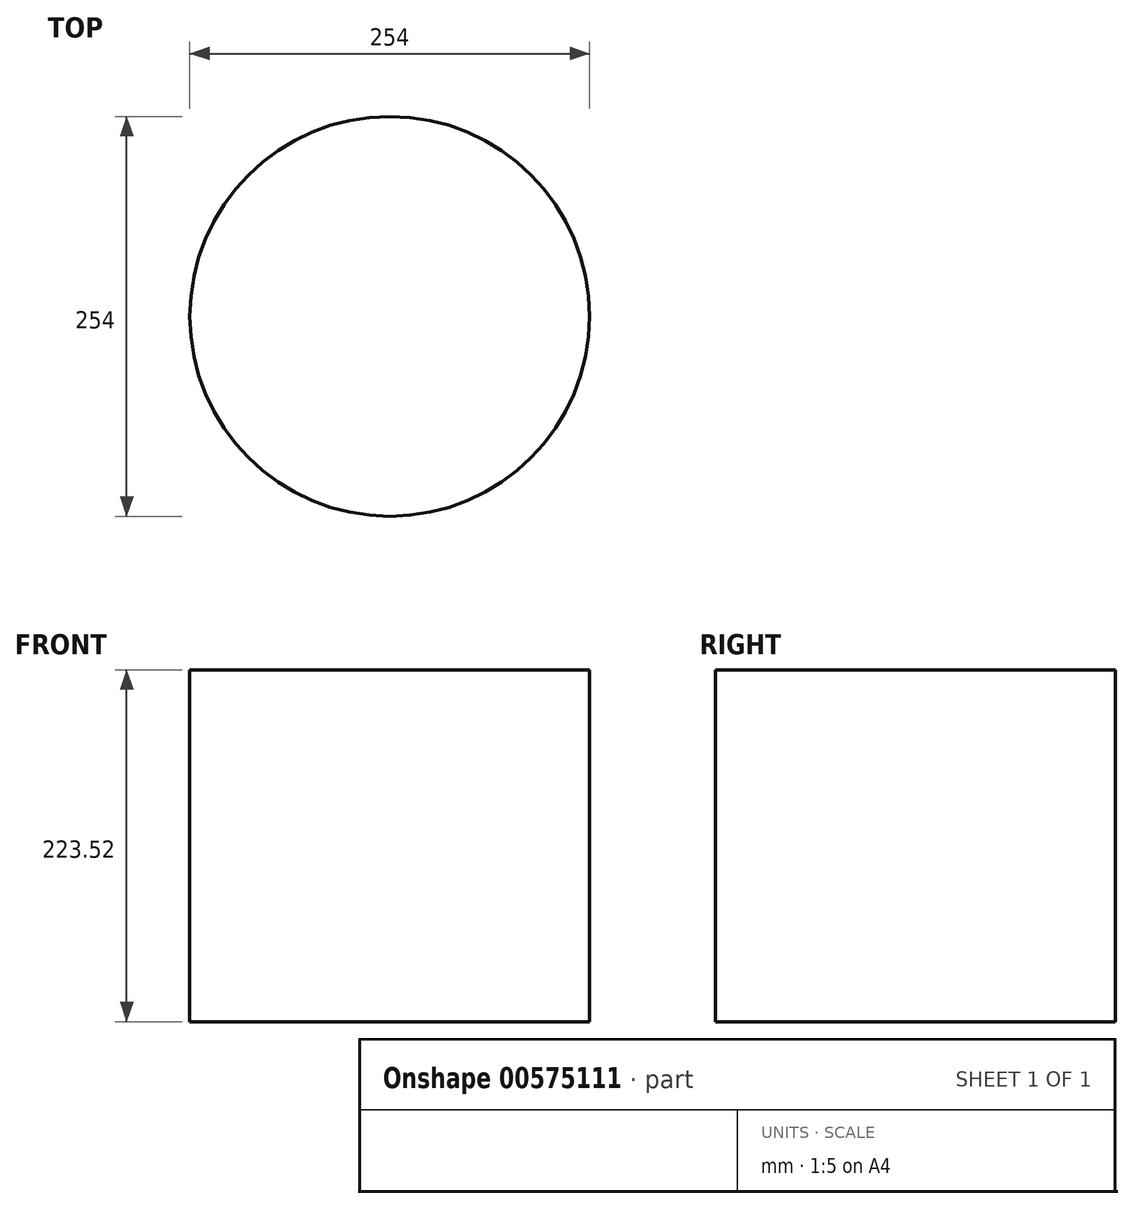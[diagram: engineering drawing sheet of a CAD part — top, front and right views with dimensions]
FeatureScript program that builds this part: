
annotation { "Feature Type Name" : "Feature", "Feature Type Description" : "" }
export const myFeature = defineFeature(function(context is Context, id is Id, definition is map)
    precondition{}
    {
        {
            var Q0;
            Q0=qCreatedBy(makeId("Top.planeOp"),FACE);
            var sketch = newSketch(context, id + "F0", { "sketchPlane" : qUnion([Q0])});
            skCircle(sketch, "E0", {"center": v(0, 0) * mm, "radius": 127 * mm});
            skSolve(sketch);
        }
        {
            var Q0;
            Q0=makeQuery(id+"F0.imprint","IMPRINT",FACE,{"disambiguationData":[TD([[makeQuery(id+"F0.imprint","IMPRINT",EDGE,{"derivedFrom":sQuery(id+"F0.wireOp",EDGE,"E0")}),1.0]])]});
            extrude(context, id + "F1", {"entities" : qUnion([Q0]), "endBound" : BoundingType.SYMMETRIC, "depth" : 223.52 * mm, "offsetDistance" : 25.4 * mm});
        }
    });
